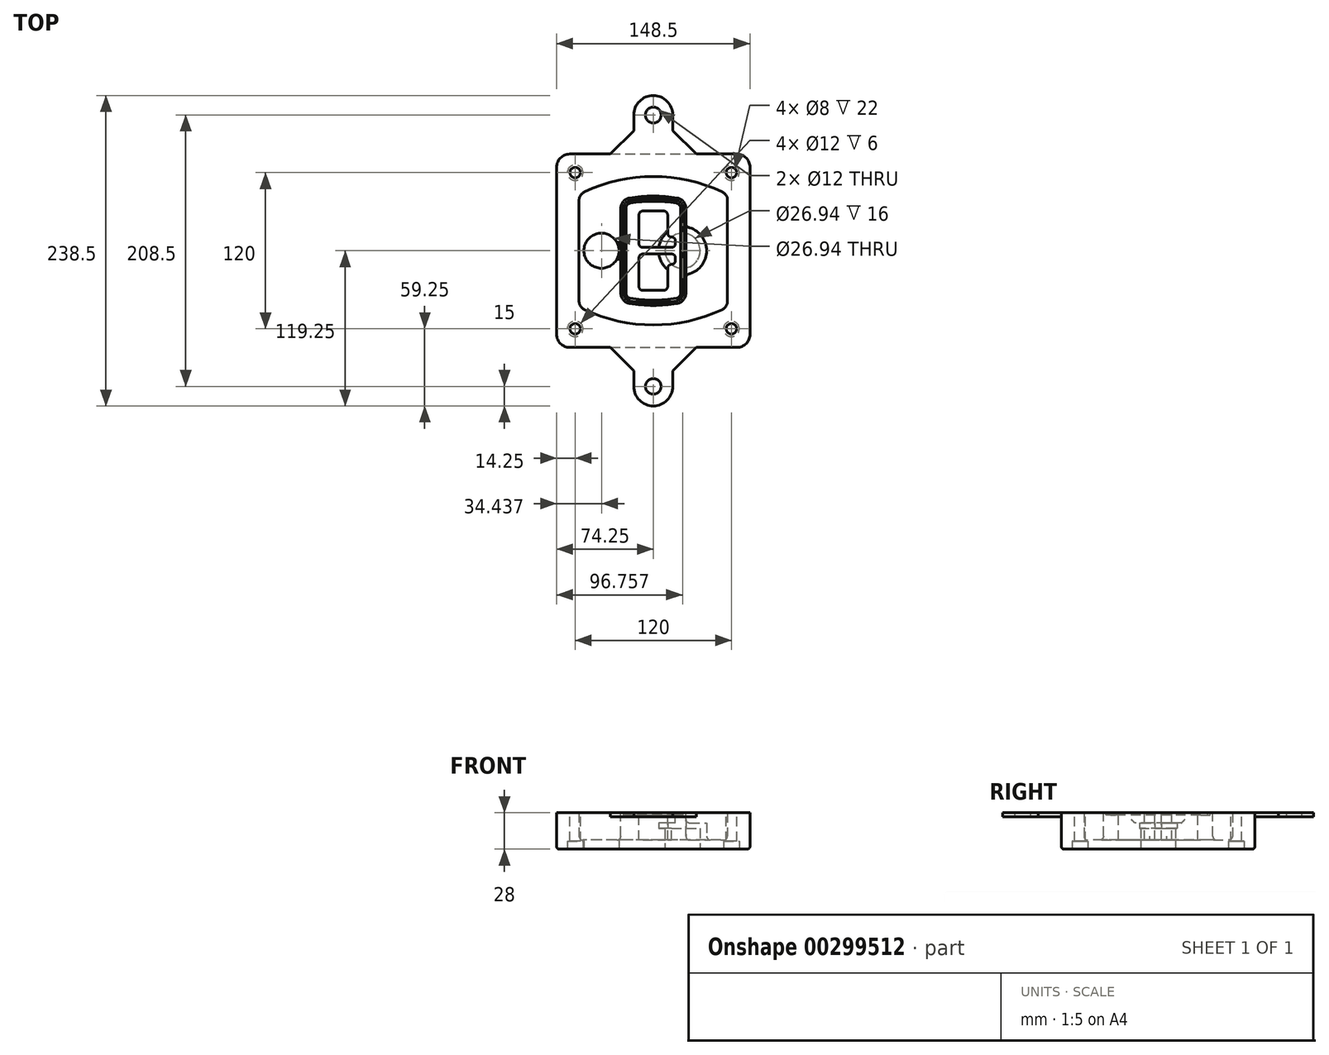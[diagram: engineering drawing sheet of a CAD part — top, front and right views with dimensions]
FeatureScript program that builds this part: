
annotation { "Feature Type Name" : "Feature", "Feature Type Description" : "" }
export const myFeature = defineFeature(function(context is Context, id is Id, definition is map)
    precondition{}
    {
        {
            var Q0;
            Q0=qCreatedBy(makeId("Top.planeOp"),FACE);
            var sketch = newSketch(context, id + "F0", { "sketchPlane" : qUnion([Q0])});
            skPoint(sketch, "E0.rect.middle", {"position": v(0, 0) * mm});
            skLineSegment(sketch, "E1.bottom", {"start": v(-64.25, -74.25) * mm, "end": v(64.25, -74.25) * mm});
            skLineSegment(sketch, "E1.top", {"start": v(-64.25, 74.25) * mm, "end": v(64.25, 74.25) * mm});
            skLineSegment(sketch, "E1.left", {"start": v(-74.25, -64.25) * mm, "end": v(-74.25, 64.25) * mm});
            skLineSegment(sketch, "E1.right", {"start": v(74.25, -64.25) * mm, "end": v(74.25, 64.25) * mm});
            skLineSegment(sketch, "E2", {"start": v(-74.25, 74.25) * mm, "end": v(74.25, -74.25) * mm, "construction": true});
            skLineSegment(sketch, "E3", {"start": v(74.25, 74.25) * mm, "end": v(-74.25, -74.25) * mm, "construction": true});
            skCircle(sketch, "E4", {"center": v(-60, 60) * mm, "radius": 4 * mm});
            skCircle(sketch, "E5", {"center": v(60, 60) * mm, "radius": 4 * mm});
            skCircle(sketch, "E6", {"center": v(60, -60) * mm, "radius": 4 * mm});
            skCircle(sketch, "E7", {"center": v(-60, -60) * mm, "radius": 4 * mm});
            skLineSegment(sketch, "E8", {"start": v(-60, 60) * mm, "end": v(60, 60) * mm, "construction": true});
            skLineSegment(sketch, "E9", {"start": v(60, 60) * mm, "end": v(60, -60) * mm, "construction": true});
            skLineSegment(sketch, "E10", {"start": v(60, -60) * mm, "end": v(-60, -60) * mm, "construction": true});
            skLineSegment(sketch, "E11", {"start": v(-60, -60) * mm, "end": v(-60, 60) * mm, "construction": true});
            skLineSegment(sketch, "E12", {"start": v(-60, 38.83) * mm, "end": v(-60, -38.83) * mm});
            skLineSegment(sketch, "E13", {"start": v(60, 38.83) * mm, "end": v(60, -38.83) * mm});
            skArc(sketch, "E14", {"start": v(54.26, 47.88) * mm, "mid": v(0, 60) * mm, "end": v(-54.26, 47.88) * mm});
            skArc(sketch, "E15", {"start": v(-54.26, -47.88) * mm, "mid": v(0, -60) * mm, "end": v(54.26, -47.88) * mm});
            skLineSegment(sketch, "E16", {"start": v(-60, 0) * mm, "end": v(60, 0) * mm, "construction": true});
            skPoint(sketch, "E17.visualSharp", {"position": v(-60, -45) * mm});
            skArc(sketch, "E17.filletArc", {"start": v(-60, -38.83) * mm, "mid": v(-58.44, -44.2) * mm, "end": v(-54.26, -47.88) * mm});
            skPoint(sketch, "E18.visualSharp", {"position": v(-60, 45) * mm});
            skArc(sketch, "E18.filletArc", {"start": v(-54.26, 47.88) * mm, "mid": v(-58.44, 44.2) * mm, "end": v(-60, 38.83) * mm});
            skPoint(sketch, "E19.visualSharp", {"position": v(60, 45) * mm});
            skArc(sketch, "E19.filletArc", {"start": v(60, 38.83) * mm, "mid": v(58.44, 44.2) * mm, "end": v(54.26, 47.88) * mm});
            skPoint(sketch, "E20.visualSharp", {"position": v(60, -45) * mm});
            skArc(sketch, "E20.filletArc", {"start": v(54.26, -47.88) * mm, "mid": v(58.44, -44.2) * mm, "end": v(60, -38.83) * mm});
            skPoint(sketch, "E21.visualSharp", {"position": v(-74.25, 74.25) * mm});
            skArc(sketch, "E21.filletArc", {"start": v(-64.25, 74.25) * mm, "mid": v(-71.32, 71.32) * mm, "end": v(-74.25, 64.25) * mm});
            skPoint(sketch, "E22.visualSharp", {"position": v(74.25, 74.25) * mm});
            skArc(sketch, "E22.filletArc", {"start": v(74.25, 64.25) * mm, "mid": v(71.32, 71.32) * mm, "end": v(64.25, 74.25) * mm});
            skPoint(sketch, "E23.visualSharp", {"position": v(74.25, -74.25) * mm});
            skArc(sketch, "E23.filletArc", {"start": v(64.25, -74.25) * mm, "mid": v(71.32, -71.32) * mm, "end": v(74.25, -64.25) * mm});
            skPoint(sketch, "E24.visualSharp", {"position": v(-74.25, -74.25) * mm});
            skArc(sketch, "E24.filletArc", {"start": v(-74.25, -64.25) * mm, "mid": v(-71.32, -71.32) * mm, "end": v(-64.25, -74.25) * mm});
            skArc(sketch, "E25.0", {"start": v(57, 38.83) * mm, "mid": v(55.9, 42.58) * mm, "end": v(52.98, 45.17) * mm});
            skLineSegment(sketch, "E25.1", {"start": v(57, 38.83) * mm, "end": v(57, -38.83) * mm});
            skArc(sketch, "E25.2", {"start": v(52.98, -45.17) * mm, "mid": v(55.9, -42.58) * mm, "end": v(57, -38.83) * mm});
            skArc(sketch, "E25.3", {"start": v(-52.98, -45.17) * mm, "mid": v(0, -57) * mm, "end": v(52.98, -45.17) * mm});
            skArc(sketch, "E25.4", {"start": v(-57, -38.83) * mm, "mid": v(-55.9, -42.58) * mm, "end": v(-52.98, -45.17) * mm});
            skArc(sketch, "E25.5", {"start": v(52.98, 45.17) * mm, "mid": v(0, 57) * mm, "end": v(-52.98, 45.17) * mm});
            skLineSegment(sketch, "E25.6", {"start": v(-57, 38.83) * mm, "end": v(-57, -38.83) * mm});
            skArc(sketch, "E25.7", {"start": v(-52.98, 45.17) * mm, "mid": v(-55.9, 42.58) * mm, "end": v(-57, 38.83) * mm});
            skArc(sketch, "E26.0", {"start": v(-55.96, 51.5) * mm, "mid": v(-61.82, 46.33) * mm, "end": v(-64, 38.83) * mm});
            skArc(sketch, "E26.1", {"start": v(55.96, 51.5) * mm, "mid": v(0, 64) * mm, "end": v(-55.96, 51.5) * mm});
            skArc(sketch, "E26.2", {"start": v(64, 38.83) * mm, "mid": v(61.82, 46.33) * mm, "end": v(55.96, 51.5) * mm});
            skLineSegment(sketch, "E26.3", {"start": v(64, 38.83) * mm, "end": v(64, -38.83) * mm});
            skArc(sketch, "E26.4", {"start": v(55.96, -51.5) * mm, "mid": v(61.82, -46.33) * mm, "end": v(64, -38.83) * mm});
            skLineSegment(sketch, "E26.5", {"start": v(-64, 38.83) * mm, "end": v(-64, -38.83) * mm});
            skArc(sketch, "E26.6", {"start": v(-55.96, -51.5) * mm, "mid": v(0, -64) * mm, "end": v(55.96, -51.5) * mm});
            skArc(sketch, "E26.7", {"start": v(-64, -38.83) * mm, "mid": v(-61.82, -46.33) * mm, "end": v(-55.96, -51.5) * mm});
            skSolve(sketch);
        }
        {
            var Q0;
            Q0=makeQuery(id+"F0.imprint","IMPRINT",FACE,{"disambiguationData":[TD([[makeQuery(id+"F0.imprint","IMPRINT",EDGE,{"derivedFrom":sQuery(id+"F0.wireOp",EDGE,"E1.bottom")}),1.0]])]});
            var Q1;
            Q1=makeQuery(id+"F0.imprint","IMPRINT",FACE,{"disambiguationData":[TD([[makeQuery(id+"F0.imprint","IMPRINT",EDGE,{"derivedFrom":sQuery(id+"F0.wireOp",EDGE,"E12")}),1.0]])]});
            var Q2;
            Q2=makeQuery(id+"F0.imprint","IMPRINT",FACE,{"disambiguationData":[TD([[makeQuery(id+"F0.imprint","IMPRINT",EDGE,{"derivedFrom":sQuery(id+"F0.wireOp",EDGE,"E25.0")}),1.0]])]});
            var Q3;
            Q3=makeQuery(id+"F0.imprint","IMPRINT",FACE,{"disambiguationData":[TD([[makeQuery(id+"F0.imprint","IMPRINT",EDGE,{"derivedFrom":sQuery(id+"F0.wireOp",EDGE,"E12")}),-1.0]])]});
            extrude(context, id + "F1", {"entities" : qUnion([Q0, Q1, Q2, Q3]), "oppositeDirection" : true, "depth" : 25 * mm});
        }
        {
            var Q0;
            Q0=makeQuery(id+"F0.imprint","IMPRINT",FACE,{"disambiguationData":[TD([[makeQuery(id+"F0.imprint","IMPRINT",EDGE,{"derivedFrom":sQuery(id+"F0.wireOp",EDGE,"E12")}),1.0]])]});
            extrude(context, id + "F2", {"entities" : qUnion([Q0]), "operationType" : NewBodyOperationType.ADD, "depth" : 3 * mm});
        }
        {
            var Q0;
            Q0=makeQuery(id+"F0.imprint","IMPRINT",FACE,{"disambiguationData":[TD([[makeQuery(id+"F0.imprint","IMPRINT",EDGE,{"derivedFrom":sQuery(id+"F0.wireOp",EDGE,"E25.0")}),1.0]])]});
            extrude(context, id + "F3", {"entities" : qUnion([Q0]), "operationType" : NewBodyOperationType.REMOVE, "oppositeDirection" : true, "depth" : 18 * mm});
        }
        {
            var Q0;
            Q0=makeQuery(id+"F2.opExtrude","CAP_FACE",FACE,{"disambiguationData":[OSD([sQuery(id+"F0.wireOp",EDGE,"E12"),sQuery(id+"F0.wireOp",EDGE,"E13"),sQuery(id+"F0.wireOp",EDGE,"E14"),sQuery(id+"F0.wireOp",EDGE,"E15"),sQuery(id+"F0.wireOp",EDGE,"E17.filletArc"),sQuery(id+"F0.wireOp",EDGE,"E18.filletArc"),sQuery(id+"F0.wireOp",EDGE,"E19.filletArc"),sQuery(id+"F0.wireOp",EDGE,"E20.filletArc"),sQuery(id+"F0.wireOp",EDGE,"E25.0"),sQuery(id+"F0.wireOp",EDGE,"E25.1"),sQuery(id+"F0.wireOp",EDGE,"E25.2"),sQuery(id+"F0.wireOp",EDGE,"E25.3"),sQuery(id+"F0.wireOp",EDGE,"E25.4"),sQuery(id+"F0.wireOp",EDGE,"E25.5"),sQuery(id+"F0.wireOp",EDGE,"E25.6"),sQuery(id+"F0.wireOp",EDGE,"E25.7")])],"isStart":false});
            var sketch = newSketch(context, id + "F4", { "sketchPlane" : qUnion([Q0])});
            skArc(sketch, "E27.0", {"start": v(-18.34, -40.45) * mm, "mid": v(0, -42) * mm, "end": v(18.34, -40.45) * mm});
            skArc(sketch, "E28.0", {"start": v(18.34, 40.45) * mm, "mid": v(0, 42) * mm, "end": v(-18.34, 40.45) * mm});
            skLineSegment(sketch, "E29", {"start": v(-25, 32.57) * mm, "end": v(-25, -32.57) * mm});
            skLineSegment(sketch, "E30", {"start": v(25, 32.57) * mm, "end": v(25, -32.57) * mm});
            skLineSegment(sketch, "E31", {"start": v(-25, 39.1) * mm, "end": v(25, 39.1) * mm, "construction": true});
            skLineSegment(sketch, "E32", {"start": v(-25, -39.1) * mm, "end": v(25, -39.1) * mm, "construction": true});
            skPoint(sketch, "E33.visualSharp", {"position": v(-25, 39.1) * mm});
            skArc(sketch, "E33.filletArc", {"start": v(-18.34, 40.45) * mm, "mid": v(-23.11, 37.73) * mm, "end": v(-25, 32.57) * mm});
            skPoint(sketch, "E34.visualSharp", {"position": v(25, 39.1) * mm});
            skArc(sketch, "E34.filletArc", {"start": v(25, 32.57) * mm, "mid": v(23.11, 37.73) * mm, "end": v(18.34, 40.45) * mm});
            skPoint(sketch, "E35.visualSharp", {"position": v(25, -39.1) * mm});
            skArc(sketch, "E35.filletArc", {"start": v(18.34, -40.45) * mm, "mid": v(23.11, -37.73) * mm, "end": v(25, -32.57) * mm});
            skPoint(sketch, "E36.visualSharp", {"position": v(-25, -39.1) * mm});
            skArc(sketch, "E36.filletArc", {"start": v(-25, -32.57) * mm, "mid": v(-23.11, -37.73) * mm, "end": v(-18.34, -40.45) * mm});
            skArc(sketch, "E37.0", {"start": v(52.98, 45.17) * mm, "mid": v(0, 57) * mm, "end": v(-52.98, 45.17) * mm});
            skArc(sketch, "E37.1", {"start": v(-52.98, 45.17) * mm, "mid": v(-55.9, 42.58) * mm, "end": v(-57, 38.83) * mm});
            skLineSegment(sketch, "E37.2", {"start": v(-57, 38.83) * mm, "end": v(-57, -38.83) * mm});
            skArc(sketch, "E37.3", {"start": v(-57, -38.83) * mm, "mid": v(-55.9, -42.58) * mm, "end": v(-52.98, -45.17) * mm});
            skArc(sketch, "E37.4", {"start": v(-52.98, -45.17) * mm, "mid": v(0, -57) * mm, "end": v(52.98, -45.17) * mm});
            skArc(sketch, "E37.5", {"start": v(52.98, -45.17) * mm, "mid": v(55.9, -42.58) * mm, "end": v(57, -38.83) * mm});
            skLineSegment(sketch, "E37.6", {"start": v(57, 38.83) * mm, "end": v(57, -38.83) * mm});
            skArc(sketch, "E37.7", {"start": v(57, 38.83) * mm, "mid": v(55.9, 42.58) * mm, "end": v(52.98, 45.17) * mm});
            skLineSegment(sketch, "E38.0", {"start": v(23, 32.57) * mm, "end": v(23, -32.57) * mm});
            skArc(sketch, "E38.1", {"start": v(18, -38.48) * mm, "mid": v(21.58, -36.44) * mm, "end": v(23, -32.57) * mm});
            skArc(sketch, "E38.2", {"start": v(-18, -38.48) * mm, "mid": v(0, -40) * mm, "end": v(18, -38.48) * mm});
            skArc(sketch, "E38.3", {"start": v(-23, -32.57) * mm, "mid": v(-21.58, -36.44) * mm, "end": v(-18, -38.48) * mm});
            skLineSegment(sketch, "E38.4", {"start": v(-23, 32.57) * mm, "end": v(-23, -32.57) * mm});
            skArc(sketch, "E38.5", {"start": v(23, 32.57) * mm, "mid": v(21.58, 36.44) * mm, "end": v(18, 38.48) * mm});
            skArc(sketch, "E38.6", {"start": v(-18, 38.48) * mm, "mid": v(-21.58, 36.44) * mm, "end": v(-23, 32.57) * mm});
            skArc(sketch, "E38.7", {"start": v(18, 38.48) * mm, "mid": v(0, 40) * mm, "end": v(-18, 38.48) * mm});
            skArc(sketch, "E39.0", {"start": v(21, 32.57) * mm, "mid": v(20.06, 35.15) * mm, "end": v(17.67, 36.5) * mm});
            skLineSegment(sketch, "E39.1", {"start": v(21, 32.57) * mm, "end": v(21, -32.57) * mm});
            skArc(sketch, "E39.2", {"start": v(17.67, -36.5) * mm, "mid": v(20.06, -35.15) * mm, "end": v(21, -32.57) * mm});
            skArc(sketch, "E39.3", {"start": v(-17.67, -36.5) * mm, "mid": v(0, -38) * mm, "end": v(17.67, -36.5) * mm});
            skArc(sketch, "E39.4", {"start": v(-21, -32.57) * mm, "mid": v(-20.06, -35.15) * mm, "end": v(-17.67, -36.5) * mm});
            skArc(sketch, "E39.5", {"start": v(17.67, 36.5) * mm, "mid": v(0, 38) * mm, "end": v(-17.67, 36.5) * mm});
            skLineSegment(sketch, "E39.6", {"start": v(-21, 32.57) * mm, "end": v(-21, -32.57) * mm});
            skArc(sketch, "E39.7", {"start": v(-17.67, 36.5) * mm, "mid": v(-20.06, 35.15) * mm, "end": v(-21, 32.57) * mm});
            skLineSegment(sketch, "E40", {"start": v(-25, 0) * mm, "end": v(25, 0) * mm, "construction": true});
            skLineSegment(sketch, "E41", {"start": v(-11, 5.5) * mm, "end": v(-11, 27.5) * mm});
            skLineSegment(sketch, "E42", {"start": v(-8, 30.5) * mm, "end": v(8, 30.5) * mm});
            skLineSegment(sketch, "E43", {"start": v(11, 27.5) * mm, "end": v(11, 13.5) * mm});
            skLineSegment(sketch, "E44", {"start": v(14, 10.5) * mm, "end": v(14, 10.5) * mm});
            skLineSegment(sketch, "E45", {"start": v(17, 7.5) * mm, "end": v(17, 5.5) * mm});
            skLineSegment(sketch, "E46", {"start": v(14, 2.5) * mm, "end": v(-8, 2.5) * mm});
            skPoint(sketch, "E47.visualSharp", {"position": v(-11, 30.5) * mm});
            skArc(sketch, "E47.filletArc", {"start": v(-8, 30.5) * mm, "mid": v(-10.12, 29.62) * mm, "end": v(-11, 27.5) * mm});
            skPoint(sketch, "E48.visualSharp", {"position": v(11, 30.5) * mm});
            skArc(sketch, "E48.filletArc", {"start": v(11, 27.5) * mm, "mid": v(10.12, 29.62) * mm, "end": v(8, 30.5) * mm});
            skPoint(sketch, "E49.visualSharp", {"position": v(11, 10.5) * mm});
            skArc(sketch, "E49.filletArc", {"start": v(11, 13.5) * mm, "mid": v(11.88, 11.38) * mm, "end": v(14, 10.5) * mm});
            skPoint(sketch, "E50.visualSharp", {"position": v(17, 10.5) * mm});
            skArc(sketch, "E50.filletArc", {"start": v(17, 7.5) * mm, "mid": v(16.12, 9.62) * mm, "end": v(14, 10.5) * mm});
            skPoint(sketch, "E51.visualSharp", {"position": v(17, 2.5) * mm});
            skArc(sketch, "E51.filletArc", {"start": v(14, 2.5) * mm, "mid": v(16.12, 3.38) * mm, "end": v(17, 5.5) * mm});
            skPoint(sketch, "E52.visualSharp", {"position": v(-11, 2.5) * mm});
            skArc(sketch, "E52.filletArc", {"start": v(-11, 5.5) * mm, "mid": v(-10.12, 3.38) * mm, "end": v(-8, 2.5) * mm});
            skLineSegment(sketch, "E53.0.MirrorCS", {"start": v(14, -2.5) * mm, "end": v(-8, -2.5) * mm});
            skArc(sketch, "E54.0.MirrorCS", {"start": v(-11, -5.5) * mm, "mid": v(-10.12, -3.38) * mm, "end": v(-8, -2.5) * mm});
            skLineSegment(sketch, "E55.0.MirrorCS", {"start": v(-11, -5.5) * mm, "end": v(-11, -27.5) * mm});
            skArc(sketch, "E56.0.MirrorCS", {"start": v(-8, -30.5) * mm, "mid": v(-10.12, -29.62) * mm, "end": v(-11, -27.5) * mm});
            skLineSegment(sketch, "E57.0.MirrorCS", {"start": v(-8, -30.5) * mm, "end": v(8, -30.5) * mm});
            skArc(sketch, "E58.0.MirrorCS", {"start": v(11, -27.5) * mm, "mid": v(10.12, -29.62) * mm, "end": v(8, -30.5) * mm});
            skLineSegment(sketch, "E59.0.MirrorCS", {"start": v(11, -27.5) * mm, "end": v(11, -13.5) * mm});
            skArc(sketch, "E60.0.MirrorCS", {"start": v(11, -13.5) * mm, "mid": v(11.88, -11.38) * mm, "end": v(14, -10.5) * mm});
            skArc(sketch, "E61.0.MirrorCS", {"start": v(17, -7.5) * mm, "mid": v(16.12, -9.62) * mm, "end": v(14, -10.5) * mm});
            skLineSegment(sketch, "E62.0.MirrorCS", {"start": v(17, -7.5) * mm, "end": v(17, -5.5) * mm});
            skArc(sketch, "E63.0.MirrorCS", {"start": v(14, -2.5) * mm, "mid": v(16.12, -3.38) * mm, "end": v(17, -5.5) * mm});
            skSolve(sketch);
        }
        {
            var Q0;
            Q0=makeQuery(id+"F4.imprint","IMPRINT",FACE,{"disambiguationData":[TD([[makeQuery(id+"F4.imprint","IMPRINT",EDGE,{"derivedFrom":sQuery(id+"F4.wireOp",EDGE,"E27.0")}),1.0]])]});
            var Q1;
            Q1=makeQuery(id+"F4.imprint","IMPRINT",FACE,{"disambiguationData":[TD([[makeQuery(id+"F4.imprint","IMPRINT",EDGE,{"derivedFrom":sQuery(id+"F4.wireOp",EDGE,"E38.0")}),-1.0]])]});
            var Q2;
            Q2=makeQuery(id+"F4.imprint","IMPRINT",FACE,{"disambiguationData":[TD([[makeQuery(id+"F4.imprint","IMPRINT",EDGE,{"derivedFrom":sQuery(id+"F4.wireOp",EDGE,"E39.0")}),1.0]])]});
            extrude(context, id + "F5", {"entities" : qUnion([Q0, Q1, Q2]), "operationType" : NewBodyOperationType.ADD, "endBound" : BoundingType.UP_TO_NEXT, "oppositeDirection" : true, "depth" : 25 * mm});
        }
        {
            var Q0;
            Q0=makeQuery(id+"F4.imprint","IMPRINT",FACE,{"disambiguationData":[TD([[makeQuery(id+"F4.imprint","IMPRINT",EDGE,{"derivedFrom":sQuery(id+"F4.wireOp",EDGE,"E38.0")}),-1.0]])]});
            extrude(context, id + "F6", {"entities" : qUnion([Q0]), "operationType" : NewBodyOperationType.REMOVE, "oppositeDirection" : true, "depth" : 2 * mm});
        }
        {
            var Q0;
            Q0=makeQuery(id+"F1.opExtrude","CAP_FACE",FACE,{"disambiguationData":[OSD([sQuery(id+"F0.wireOp",EDGE,"E1.bottom"),sQuery(id+"F0.wireOp",EDGE,"E1.top"),sQuery(id+"F0.wireOp",EDGE,"E1.left"),sQuery(id+"F0.wireOp",EDGE,"E1.right"),sQuery(id+"F0.wireOp",EDGE,"E4"),sQuery(id+"F0.wireOp",EDGE,"E5"),sQuery(id+"F0.wireOp",EDGE,"E6"),sQuery(id+"F0.wireOp",EDGE,"E7"),sQuery(id+"F0.wireOp",EDGE,"E21.filletArc"),sQuery(id+"F0.wireOp",EDGE,"E22.filletArc"),sQuery(id+"F0.wireOp",EDGE,"E23.filletArc"),sQuery(id+"F0.wireOp",EDGE,"E24.filletArc")])],"isStart":false});
            var sketch = newSketch(context, id + "F7", { "sketchPlane" : qUnion([Q0])});
            skCircle(sketch, "E64", {"center": v(22.5, 0) * mm, "radius": 13.47 * mm});
            skCircle(sketch, "E65", {"center": v(-39.81, 0) * mm, "radius": 13.47 * mm});
            skLineSegment(sketch, "E66", {"start": v(74.25, 0) * mm, "end": v(-74.25, 0) * mm});
            skCircle(sketch, "E67", {"center": v(22.5, 0) * mm, "radius": 18.47 * mm});
            skCircle(sketch, "E68", {"center": v(60, -60) * mm, "radius": 6 * mm});
            skCircle(sketch, "E69", {"center": v(-60, -60) * mm, "radius": 6 * mm});
            skCircle(sketch, "E70", {"center": v(-60, 60) * mm, "radius": 6 * mm});
            skCircle(sketch, "E71", {"center": v(60, 60) * mm, "radius": 6 * mm});
            skSolve(sketch);
        }
        {
            var Q0;
            {var subQ1=sQuery(id+"F7.wireOp",EDGE,"E66");var subQ4=sQuery(id+"F7.wireOp",EDGE,"E64");var subQ6=makeQuery(id+"F7.imprint","INTERSECT",VERTEX,{"disambiguationData":[OD(0.0)],"derivedFrom":[subQ4,subQ1]});Q0=makeQuery(id+"F7.imprint","IMPRINT",FACE,{"disambiguationData":[TD([[makeQuery(id+"F7.imprint","IMPRINT",EDGE,{"disambiguationData":[TD([[subQ6,-1.0]])],"derivedFrom":subQ4}),-1.0]])]});}
            var Q1;
            {var subQ0=sQuery(id+"F7.wireOp",EDGE,"E66");var subQ1=sQuery(id+"F7.wireOp",EDGE,"E64");var subQ3=makeQuery(id+"F7.imprint","INTERSECT",VERTEX,{"disambiguationData":[OD(0.0)],"derivedFrom":[subQ1,subQ0]});Q1=makeQuery(id+"F7.imprint","IMPRINT",FACE,{"disambiguationData":[TD([[makeQuery(id+"F7.imprint","IMPRINT",EDGE,{"disambiguationData":[TD([[subQ3,-1.0]])],"derivedFrom":subQ1}),1.0]])]});}
            var Q2;
            {var subQ0=sQuery(id+"F7.wireOp",EDGE,"E66");var subQ1=sQuery(id+"F7.wireOp",EDGE,"E64");var subQ3=makeQuery(id+"F7.imprint","INTERSECT",VERTEX,{"disambiguationData":[OD(0.0)],"derivedFrom":[subQ1,subQ0]});Q2=makeQuery(id+"F7.imprint","IMPRINT",FACE,{"disambiguationData":[TD([[makeQuery(id+"F7.imprint","IMPRINT",EDGE,{"disambiguationData":[TD([[subQ3,1.0]])],"derivedFrom":subQ1}),1.0]])]});}
            var Q3;
            {var subQ1=sQuery(id+"F7.wireOp",EDGE,"E66");var subQ4=sQuery(id+"F7.wireOp",EDGE,"E64");var subQ6=makeQuery(id+"F7.imprint","INTERSECT",VERTEX,{"disambiguationData":[OD(0.0)],"derivedFrom":[subQ4,subQ1]});Q3=makeQuery(id+"F7.imprint","IMPRINT",FACE,{"disambiguationData":[TD([[makeQuery(id+"F7.imprint","IMPRINT",EDGE,{"disambiguationData":[TD([[subQ6,1.0]])],"derivedFrom":subQ4}),-1.0]])]});}
            extrude(context, id + "F8", {"entities" : qUnion([Q0, Q1, Q2, Q3]), "operationType" : NewBodyOperationType.ADD, "oppositeDirection" : true, "depth" : 20 * mm});
        }
        {
            var Q0;
            {var subQ0=sQuery(id+"F7.wireOp",EDGE,"E66");var subQ1=sQuery(id+"F7.wireOp",EDGE,"E64");var subQ3=makeQuery(id+"F7.imprint","INTERSECT",VERTEX,{"disambiguationData":[OD(0.0)],"derivedFrom":[subQ1,subQ0]});Q0=makeQuery(id+"F7.imprint","IMPRINT",FACE,{"disambiguationData":[TD([[makeQuery(id+"F7.imprint","IMPRINT",EDGE,{"disambiguationData":[TD([[subQ3,-1.0]])],"derivedFrom":subQ1}),1.0]])]});}
            var Q1;
            {var subQ0=sQuery(id+"F7.wireOp",EDGE,"E66");var subQ1=sQuery(id+"F7.wireOp",EDGE,"E64");var subQ3=makeQuery(id+"F7.imprint","INTERSECT",VERTEX,{"disambiguationData":[OD(0.0)],"derivedFrom":[subQ1,subQ0]});Q1=makeQuery(id+"F7.imprint","IMPRINT",FACE,{"disambiguationData":[TD([[makeQuery(id+"F7.imprint","IMPRINT",EDGE,{"disambiguationData":[TD([[subQ3,1.0]])],"derivedFrom":subQ1}),1.0]])]});}
            extrude(context, id + "F9", {"entities" : qUnion([Q0, Q1]), "operationType" : NewBodyOperationType.REMOVE, "oppositeDirection" : true, "depth" : 16 * mm});
        }
        {
            var Q0;
            {var subQ0=sQuery(id+"F7.wireOp",EDGE,"E66");var subQ1=sQuery(id+"F7.wireOp",EDGE,"E65");var subQ3=makeQuery(id+"F7.imprint","INTERSECT",VERTEX,{"disambiguationData":[OD(0.0)],"derivedFrom":[subQ1,subQ0]});Q0=makeQuery(id+"F7.imprint","IMPRINT",FACE,{"disambiguationData":[TD([[makeQuery(id+"F7.imprint","IMPRINT",EDGE,{"disambiguationData":[TD([[subQ3,-1.0]])],"derivedFrom":subQ1}),1.0]])]});}
            var Q1;
            {var subQ0=sQuery(id+"F7.wireOp",EDGE,"E66");var subQ1=sQuery(id+"F7.wireOp",EDGE,"E65");var subQ3=makeQuery(id+"F7.imprint","INTERSECT",VERTEX,{"disambiguationData":[OD(0.0)],"derivedFrom":[subQ1,subQ0]});Q1=makeQuery(id+"F7.imprint","IMPRINT",FACE,{"disambiguationData":[TD([[makeQuery(id+"F7.imprint","IMPRINT",EDGE,{"disambiguationData":[TD([[subQ3,1.0]])],"derivedFrom":subQ1}),1.0]])]});}
            extrude(context, id + "F10", {"entities" : qUnion([Q0, Q1]), "operationType" : NewBodyOperationType.REMOVE, "oppositeDirection" : true, "depth" : 25 * mm});
        }
        {
            var Q0;
            Q0=makeQuery(id+"F7.imprint","IMPRINT",FACE,{"disambiguationData":[TD([[makeQuery(id+"F7.imprint","IMPRINT",EDGE,{"derivedFrom":sQuery(id+"F7.wireOp",EDGE,"E68")}),1.0]])]});
            var Q1;
            Q1=makeQuery(id+"F7.imprint","IMPRINT",FACE,{"disambiguationData":[TD([[makeQuery(id+"F7.imprint","IMPRINT",EDGE,{"derivedFrom":makeQuery(id+"F1.opExtrude","CAP_EDGE",EDGE,{"disambiguationData":[OSD([sQuery(id+"F0.wireOp",EDGE,"E5")])],"isStart":false})}),-1.0]])]});
            var Q2;
            Q2=makeQuery(id+"F7.imprint","IMPRINT",FACE,{"disambiguationData":[TD([[makeQuery(id+"F7.imprint","IMPRINT",EDGE,{"derivedFrom":sQuery(id+"F7.wireOp",EDGE,"E69")}),1.0]])]});
            var Q3;
            Q3=makeQuery(id+"F7.imprint","IMPRINT",FACE,{"disambiguationData":[TD([[makeQuery(id+"F7.imprint","IMPRINT",EDGE,{"derivedFrom":makeQuery(id+"F1.opExtrude","CAP_EDGE",EDGE,{"disambiguationData":[OSD([sQuery(id+"F0.wireOp",EDGE,"E4")])],"isStart":false})}),-1.0]])]});
            var Q4;
            Q4=makeQuery(id+"F7.imprint","IMPRINT",FACE,{"disambiguationData":[TD([[makeQuery(id+"F7.imprint","IMPRINT",EDGE,{"derivedFrom":sQuery(id+"F7.wireOp",EDGE,"E70")}),1.0]])]});
            var Q5;
            Q5=makeQuery(id+"F7.imprint","IMPRINT",FACE,{"disambiguationData":[TD([[makeQuery(id+"F7.imprint","IMPRINT",EDGE,{"derivedFrom":makeQuery(id+"F1.opExtrude","CAP_EDGE",EDGE,{"disambiguationData":[OSD([sQuery(id+"F0.wireOp",EDGE,"E7")])],"isStart":false})}),-1.0]])]});
            var Q6;
            Q6=makeQuery(id+"F7.imprint","IMPRINT",FACE,{"disambiguationData":[TD([[makeQuery(id+"F7.imprint","IMPRINT",EDGE,{"derivedFrom":sQuery(id+"F7.wireOp",EDGE,"E71")}),1.0]])]});
            var Q7;
            Q7=makeQuery(id+"F7.imprint","IMPRINT",FACE,{"disambiguationData":[TD([[makeQuery(id+"F7.imprint","IMPRINT",EDGE,{"derivedFrom":makeQuery(id+"F1.opExtrude","CAP_EDGE",EDGE,{"disambiguationData":[OSD([sQuery(id+"F0.wireOp",EDGE,"E6")])],"isStart":false})}),-1.0]])]});
            extrude(context, id + "F11", {"entities" : qUnion([Q0, Q1, Q2, Q3, Q4, Q5, Q6, Q7]), "operationType" : NewBodyOperationType.REMOVE, "oppositeDirection" : true, "depth" : 6 * mm});
        }
        {
            var Q0;
            Q0=makeQuery(id+"F9.boolean.opBoolean","COPY",FACE,{"derivedFrom":makeQuery(id+"F9.opExtrude","CAP_FACE",FACE,{"disambiguationData":[OSD([sQuery(id+"F7.wireOp",EDGE,"E64")])],"isStart":false})});
            var sketch = newSketch(context, id + "F12", { "sketchPlane" : qUnion([Q0])});
            skArc(sketch, "E72.0", {"start": v(11, 14.45) * mm, "mid": v(6.45, 9.13) * mm, "end": v(4.2, 2.5) * mm});
            skArc(sketch, "E72.1", {"start": v(4.2, -2.5) * mm, "mid": v(6.45, -9.13) * mm, "end": v(11, -14.45) * mm});
            skLineSegment(sketch, "E73", {"start": v(4.2, -2.5) * mm, "end": v(14, -2.5) * mm});
            skLineSegment(sketch, "E74.0", {"start": v(14, 2.5) * mm, "end": v(4.2, 2.5) * mm});
            skArc(sketch, "E74.1", {"start": v(14, 2.5) * mm, "mid": v(16.12, 3.38) * mm, "end": v(17, 5.5) * mm});
            skLineSegment(sketch, "E74.2", {"start": v(17, 7.5) * mm, "end": v(17, 5.5) * mm});
            skArc(sketch, "E74.3", {"start": v(17, 7.5) * mm, "mid": v(16.12, 9.62) * mm, "end": v(14, 10.5) * mm});
            skArc(sketch, "E74.4", {"start": v(11, 13.5) * mm, "mid": v(11.88, 11.38) * mm, "end": v(14, 10.5) * mm});
            skLineSegment(sketch, "E74.5", {"start": v(11, 14.45) * mm, "end": v(11, 13.5) * mm});
            skLineSegment(sketch, "E74.7", {"start": v(14, -2.5) * mm, "end": v(4.2, -2.5) * mm});
            skArc(sketch, "E74.8", {"start": v(14, -2.5) * mm, "mid": v(16.12, -3.38) * mm, "end": v(17, -5.5) * mm});
            skLineSegment(sketch, "E74.9", {"start": v(17, -7.5) * mm, "end": v(17, -5.5) * mm});
            skArc(sketch, "E74.10", {"start": v(17, -7.5) * mm, "mid": v(16.12, -9.62) * mm, "end": v(14, -10.5) * mm});
            skArc(sketch, "E74.11", {"start": v(11, -13.5) * mm, "mid": v(11.88, -11.38) * mm, "end": v(14, -10.5) * mm});
            skLineSegment(sketch, "E74.12", {"start": v(11, -14.45) * mm, "end": v(11, -13.5) * mm});
            skPoint(sketch, "E75.orphan", {"position": v(11, -27.5) * mm});
            skPoint(sketch, "E76.orphan", {"position": v(-8, -2.5) * mm});
            skPoint(sketch, "E77.orphan", {"position": v(-8, 2.5) * mm});
            skPoint(sketch, "E78.orphan", {"position": v(11, 27.5) * mm});
            skSolve(sketch);
        }
        {
            var Q0;
            {var subQ7=sQuery(id+"F12.wireOp",EDGE,"E72.0");var subQ14=sQuery(id+"F12.wireOp",EDGE,"E72.1");var subQ16=sQuery(id+"F12.wireOp",EDGE,"E74.1");var subQ18=sQuery(id+"F12.wireOp",EDGE,"E74.8");Q0=qUnion([makeQuery(id+"F12.imprint","IMPRINT",FACE,{"disambiguationData":[TD([[makeQuery(id+"F12.imprint","IMPRINT",EDGE,{"derivedFrom":subQ7}),1.0]])]}),makeQuery(id+"F12.imprint","IMPRINT",FACE,{"disambiguationData":[TD([[makeQuery(id+"F12.imprint","IMPRINT",EDGE,{"derivedFrom":subQ14}),1.0]])]}),makeQuery(id+"F12.imprint","IMPRINT",FACE,{"disambiguationData":[TD([[makeQuery(id+"F12.imprint","IMPRINT",EDGE,{"derivedFrom":subQ16}),1.0]])]}),makeQuery(id+"F12.imprint","IMPRINT",FACE,{"disambiguationData":[TD([[makeQuery(id+"F12.imprint","IMPRINT",EDGE,{"derivedFrom":subQ18}),-1.0]])]})]);}
            var Q1;
            Q1=makeQuery(id+"F5.boolean.opBoolean","SPLIT",FACE,{"disambiguationData":[TD([makeQuery(id+"F5.opExtrude","SWEPT_FACE",FACE,{"disambiguationData":[OSD([sQuery(id+"F4.wireOp",EDGE,"E41")])]})])],"derivedFrom":makeQuery(id+"F3.boolean.opBoolean","COPY",FACE,{"derivedFrom":makeQuery(id+"F3.opExtrude","CAP_FACE",FACE,{"disambiguationData":[OSD([sQuery(id+"F0.wireOp",EDGE,"E25.0"),sQuery(id+"F0.wireOp",EDGE,"E25.1"),sQuery(id+"F0.wireOp",EDGE,"E25.2"),sQuery(id+"F0.wireOp",EDGE,"E25.3"),sQuery(id+"F0.wireOp",EDGE,"E25.4"),sQuery(id+"F0.wireOp",EDGE,"E25.5"),sQuery(id+"F0.wireOp",EDGE,"E25.6"),sQuery(id+"F0.wireOp",EDGE,"E25.7")])],"isStart":false})})});
            extrude(context, id + "F13", {"entities" : qUnion([Q0]), "operationType" : NewBodyOperationType.REMOVE, "endBound" : BoundingType.UP_TO_SURFACE, "endBoundEntityFace" : qUnion([Q1]), "depth" : 25 * mm});
        }
        {
            var Q0;
            Q0=makeQuery(id+"F3.boolean.opBoolean","COPY",EDGE,{"derivedFrom":makeQuery(id+"F3.opExtrude","CAP_EDGE",EDGE,{"disambiguationData":[OSD([sQuery(id+"F0.wireOp",EDGE,"E25.6")])],"isStart":false})});
            var Q1;
            Q1=makeQuery(id+"F8.boolean.opBoolean","INTERSECT",EDGE,{"derivedFrom":[makeQuery(id+"F5.opExtrude","SWEPT_FACE",FACE,{"disambiguationData":[OSD([sQuery(id+"F4.wireOp",EDGE,"E30")])]}),makeQuery(id+"F8.opExtrude","CAP_FACE",FACE,{"disambiguationData":[OSD([sQuery(id+"F7.wireOp",EDGE,"E67")])],"isStart":false})]});
            var Q2;
            Q2=makeQuery(id+"F8.boolean.opBoolean","INTERSECT",EDGE,{"disambiguationData":[OD(1.0)],"derivedFrom":[makeQuery(id+"F5.opExtrude","SWEPT_FACE",FACE,{"disambiguationData":[OSD([sQuery(id+"F4.wireOp",EDGE,"E30")])]}),makeQuery(id+"F8.opExtrude","SWEPT_FACE",FACE,{"disambiguationData":[OSD([sQuery(id+"F7.wireOp",EDGE,"E67")])]})]});
            var Q3;
            {var subQ0=sQuery(id+"F4.wireOp",EDGE,"E30");Q3=makeQuery(id+"F8.boolean.opBoolean","SPLIT",EDGE,{"disambiguationData":[TD([makeQuery(id+"F5.opExtrude","SWEPT_FACE",FACE,{"disambiguationData":[OSD([sQuery(id+"F4.wireOp",EDGE,"E35.filletArc")])]})])],"derivedFrom":makeQuery(id+"F5.opExtrude","CAP_EDGE",EDGE,{"disambiguationData":[OSD([subQ0])],"isStart":false})});}
            var Q4;
            {var subQ0=sQuery(id+"F0.wireOp",EDGE,"E25.7");var subQ1=sQuery(id+"F0.wireOp",EDGE,"E25.1");var subQ2=sQuery(id+"F0.wireOp",EDGE,"E25.6");var subQ3=sQuery(id+"F0.wireOp",EDGE,"E25.5");var subQ4=sQuery(id+"F0.wireOp",EDGE,"E25.4");var subQ5=sQuery(id+"F0.wireOp",EDGE,"E25.0");var subQ6=sQuery(id+"F0.wireOp",EDGE,"E25.2");var subQ7=sQuery(id+"F0.wireOp",EDGE,"E25.3");Q4=makeQuery(id+"F8.boolean.opBoolean","INTERSECT",EDGE,{"derivedFrom":[makeQuery(id+"F5.boolean.opBoolean","SPLIT",FACE,{"disambiguationData":[TD([makeQuery(id+"F2.opExtrude","SWEPT_FACE",FACE,{"disambiguationData":[OSD([subQ5])]})])],"derivedFrom":makeQuery(id+"F3.boolean.opBoolean","COPY",FACE,{"derivedFrom":makeQuery(id+"F3.opExtrude","CAP_FACE",FACE,{"disambiguationData":[OSD([subQ5,subQ1,subQ6,subQ7,subQ4,subQ3,subQ2,subQ0])],"isStart":false})})}),makeQuery(id+"F8.opExtrude","SWEPT_FACE",FACE,{"disambiguationData":[OSD([sQuery(id+"F7.wireOp",EDGE,"E67")])]})]});}
            var Q5;
            Q5=makeQuery(id+"F8.boolean.opBoolean","INTERSECT",EDGE,{"disambiguationData":[OD(0.0)],"derivedFrom":[makeQuery(id+"F5.opExtrude","SWEPT_FACE",FACE,{"disambiguationData":[OSD([sQuery(id+"F4.wireOp",EDGE,"E30")])]}),makeQuery(id+"F8.opExtrude","SWEPT_FACE",FACE,{"disambiguationData":[OSD([sQuery(id+"F7.wireOp",EDGE,"E67")])]})]});
            fillet(context, id + "F14", {"entities" : qUnion([Q0, Q1, Q2, Q3, Q4, Q5]), "radius" : 3 * mm, "tangentPropagation" : true, "allowEdgeOverflow" : false});
        }
        {
            var Q0;
            Q0=makeQuery(id+"F1.opExtrude","CAP_EDGE",EDGE,{"disambiguationData":[OSD([sQuery(id+"F0.wireOp",EDGE,"E1.bottom")])],"isStart":false});
            fillet(context, id + "F15", {"entities" : qUnion([Q0]), "radius" : 2 * mm, "tangentPropagation" : true, "allowEdgeOverflow" : false});
        }
        {
            var Q0;
            {var subQ0=sQuery(id+"F0.wireOp",EDGE,"E21.filletArc");var subQ1=sQuery(id+"F0.wireOp",EDGE,"E7");var subQ2=sQuery(id+"F0.wireOp",EDGE,"E6");var subQ3=sQuery(id+"F0.wireOp",EDGE,"E5");var subQ4=sQuery(id+"F0.wireOp",EDGE,"E4");var subQ5=sQuery(id+"F0.wireOp",EDGE,"E22.filletArc");var subQ6=sQuery(id+"F0.wireOp",EDGE,"E1.bottom");var subQ7=sQuery(id+"F0.wireOp",EDGE,"E1.right");var subQ8=sQuery(id+"F0.wireOp",EDGE,"E1.top");var subQ9=sQuery(id+"F0.wireOp",EDGE,"E1.left");var subQ10=sQuery(id+"F0.wireOp",EDGE,"E23.filletArc");var subQ11=sQuery(id+"F0.wireOp",EDGE,"E24.filletArc");Q0=makeQuery(id+"F2.boolean.opBoolean","SPLIT",FACE,{"disambiguationData":[TD([makeQuery(id+"F1.opExtrude","SWEPT_FACE",FACE,{"disambiguationData":[OSD([subQ6])]})])],"derivedFrom":makeQuery(id+"F1.opExtrude","CAP_FACE",FACE,{"disambiguationData":[OSD([subQ6,subQ8,subQ9,subQ7,subQ4,subQ3,subQ2,subQ1,subQ0,subQ5,subQ10,subQ11])],"isStart":true})});}
            var sketch = newSketch(context, id + "F16", { "sketchPlane" : qUnion([Q0])});
            skLineSegment(sketch, "E79", {"start": v(0, 74.25) * mm, "end": v(0, 104.25) * mm, "construction": true});
            skCircle(sketch, "E80", {"center": v(0, 104.25) * mm, "radius": 6 * mm});
            skArc(sketch, "E81", {"start": v(15, 104.25) * mm, "mid": v(0, 119.25) * mm, "end": v(-15, 104.25) * mm});
            skLineSegment(sketch, "E82", {"start": v(-15, 104.25) * mm, "end": v(-15, 92.25) * mm});
            skLineSegment(sketch, "E83", {"start": v(15, 104.25) * mm, "end": v(15, 92.25) * mm});
            skLineSegment(sketch, "E84", {"start": v(-15, 92.25) * mm, "end": v(-33, 74.25) * mm});
            skLineSegment(sketch, "E85", {"start": v(15, 92.25) * mm, "end": v(33, 74.25) * mm});
            skLineSegment(sketch, "E86", {"start": v(-74.25, 0) * mm, "end": v(74.25, 0) * mm, "construction": true});
            skArc(sketch, "E87.MirrorCS", {"start": v(-15, 104.25) * mm, "mid": v(0, 119.25) * mm, "end": v(15, 104.25) * mm});
            skLineSegment(sketch, "E88.MirrorCS", {"start": v(15, -104.25) * mm, "end": v(15, -92.25) * mm});
            skLineSegment(sketch, "E89.MirrorCS", {"start": v(-15, -104.25) * mm, "end": v(-15, -92.25) * mm});
            skCircle(sketch, "E90.MirrorC", {"center": v(0, -104.25) * mm, "radius": 6 * mm});
            skLineSegment(sketch, "E91.MirrorCS", {"start": v(-15, -92.25) * mm, "end": v(-33, -74.25) * mm});
            skArc(sketch, "E92.MirrorCS", {"start": v(15, -104.25) * mm, "mid": v(0, -119.25) * mm, "end": v(-15, -104.25) * mm});
            skLineSegment(sketch, "E93.MirrorCS", {"start": v(15, -92.25) * mm, "end": v(33, -74.25) * mm});
            skLineSegment(sketch, "E94.MirrorCS", {"start": v(0, -74.25) * mm, "end": v(0, -104.25) * mm, "construction": true});
            skArc(sketch, "E95.MirrorCS", {"start": v(-15, -104.25) * mm, "mid": v(0, -119.25) * mm, "end": v(15, -104.25) * mm});
            skSolve(sketch);
        }
        {
            var Q0;
            {var subQ0=sQuery(id+"F16.wireOp",EDGE,"E85");Q0=makeQuery(id+"F16.imprint","IMPRINT",FACE,{"disambiguationData":[TD([[makeQuery(id+"F16.imprint","IMPRINT",EDGE,{"derivedFrom":subQ0}),-1.0]])]});}
            var Q1;
            Q1=makeQuery(id+"F16.imprint","IMPRINT",FACE,{"disambiguationData":[TD([[makeQuery(id+"F16.imprint","IMPRINT",EDGE,{"derivedFrom":makeQuery(id+"F1.opExtrude","CAP_EDGE",EDGE,{"disambiguationData":[OSD([sQuery(id+"F0.wireOp",EDGE,"E1.left")])],"isStart":true})}),-1.0]])]});
            var Q2;
            {var subQ1=sQuery(id+"F16.wireOp",EDGE,"E93.MirrorCS");Q2=makeQuery(id+"F16.imprint","IMPRINT",FACE,{"disambiguationData":[TD([[makeQuery(id+"F16.imprint","IMPRINT",EDGE,{"derivedFrom":subQ1}),1.0]])]});}
            var Q3;
            Q3=makeQuery(id+"F2.opExtrude","CAP_FACE",FACE,{"disambiguationData":[OSD([sQuery(id+"F0.wireOp",EDGE,"E12"),sQuery(id+"F0.wireOp",EDGE,"E13"),sQuery(id+"F0.wireOp",EDGE,"E14"),sQuery(id+"F0.wireOp",EDGE,"E15"),sQuery(id+"F0.wireOp",EDGE,"E17.filletArc"),sQuery(id+"F0.wireOp",EDGE,"E18.filletArc"),sQuery(id+"F0.wireOp",EDGE,"E19.filletArc"),sQuery(id+"F0.wireOp",EDGE,"E20.filletArc"),sQuery(id+"F0.wireOp",EDGE,"E25.0"),sQuery(id+"F0.wireOp",EDGE,"E25.1"),sQuery(id+"F0.wireOp",EDGE,"E25.2"),sQuery(id+"F0.wireOp",EDGE,"E25.3"),sQuery(id+"F0.wireOp",EDGE,"E25.4"),sQuery(id+"F0.wireOp",EDGE,"E25.5"),sQuery(id+"F0.wireOp",EDGE,"E25.6"),sQuery(id+"F0.wireOp",EDGE,"E25.7")])],"isStart":false});
            extrude(context, id + "F17", {"entities" : qUnion([Q0, Q1, Q2]), "operationType" : NewBodyOperationType.ADD, "endBound" : BoundingType.UP_TO_SURFACE, "endBoundEntityFace" : qUnion([Q3]), "depth" : 25 * mm});
        }
    });
